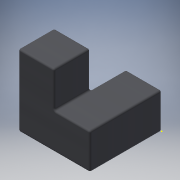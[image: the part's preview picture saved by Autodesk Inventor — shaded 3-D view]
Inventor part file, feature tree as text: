
AUTODESK INVENTOR PART (.ipt)
format: ipt  version: 2016 (Build 200138000, 138)  size: 160,256 bytes
history: native  units: in
note: dims shown in document units (in); Inventor stores cm internally (conversion verified against a paired STEP export)
features: plane x8, extrude x3, sketch x2, other x1, fillet x1
ambient origin geometry x8: Origin, YZ Plane, XZ Plane, XY Plane, X Axis, Y Axis, Z Axis, Center Point
bodies: Solid1 (feature_tree)
feature tree (15):
  other  "Cube Master.ipt"
  extrude  "Extrusion1"  Depth=0.3937in
  extrude  "Extrusion2"  TaperAngle=0.0deg  [1 undecoded]
  extrude  "Extrusion3"  Depth=0.0193in TaperAngle=0.0deg
  fillet  "Fillet1"  Radius=0.0193in
  sketch  "Sketch2"  dims[d2=1.0in d3=0.0in d4=0.0in d5=0.0in d6=1.0in d7=0.0in d9=0.0193in d10=0.0193in]
  sketch  "Sketch1"  dims[d0=0.3937in d1=0.3937in]
  plane  "Work Plane1"
  plane  "Work Plane2"
  plane  "Work Plane3"
  plane  "Work Plane4"
  plane  "Work Plane5"
  plane  "Work Plane6"
  plane  "Work Plane7"
  plane  "Work Plane8"
note: 1 required parameter value undecoded (feature->parameter linkage not recoverable at this tier; creation-order binding heuristic only, values carry confidence <= 0.55)
